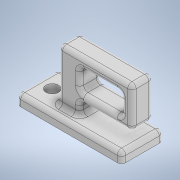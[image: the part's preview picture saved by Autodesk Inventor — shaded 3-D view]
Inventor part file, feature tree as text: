
AUTODESK INVENTOR PART (.ipt)
format: ipt  version: 2021.4 (Build 254397000, 397)  size: 249,856 bytes
history: native  units: mm
features: sketch x6, extrude x5, other x1, hole x1, fillet x1
ambient origin geometry x8: Origin, YZ Plane, XZ Plane, XY Plane, X Axis, Y Axis, Z Axis, Center Point
bodies: Body1 (feature_tree)
feature tree (14):
  other  "ソリッド1"
  extrude  "押し出し1"  Depth=20.0mm
  hole  "穴2"  [1 undecoded]
  extrude  "押し出し3"  Depth=5.0mm TaperAngle=0.0deg
  extrude  "押し出し4"  Depth=10.0mm
  extrude  "押し出し6"  Depth=7.0mm
  extrude  "押し出し7"  Depth=10.0mm
  fillet  "フィレット2"  Radius=35.0mm
  sketch  "スケッチ1"
  sketch  "スケッチ4"
  sketch  "スケッチ5"
  sketch  "スケッチ6"
  sketch  "スケッチ8"
  sketch  "スケッチ9"
note: 1 required parameter value undecoded (feature->parameter linkage not recoverable at this tier; creation-order binding heuristic only, values carry confidence <= 0.55)
